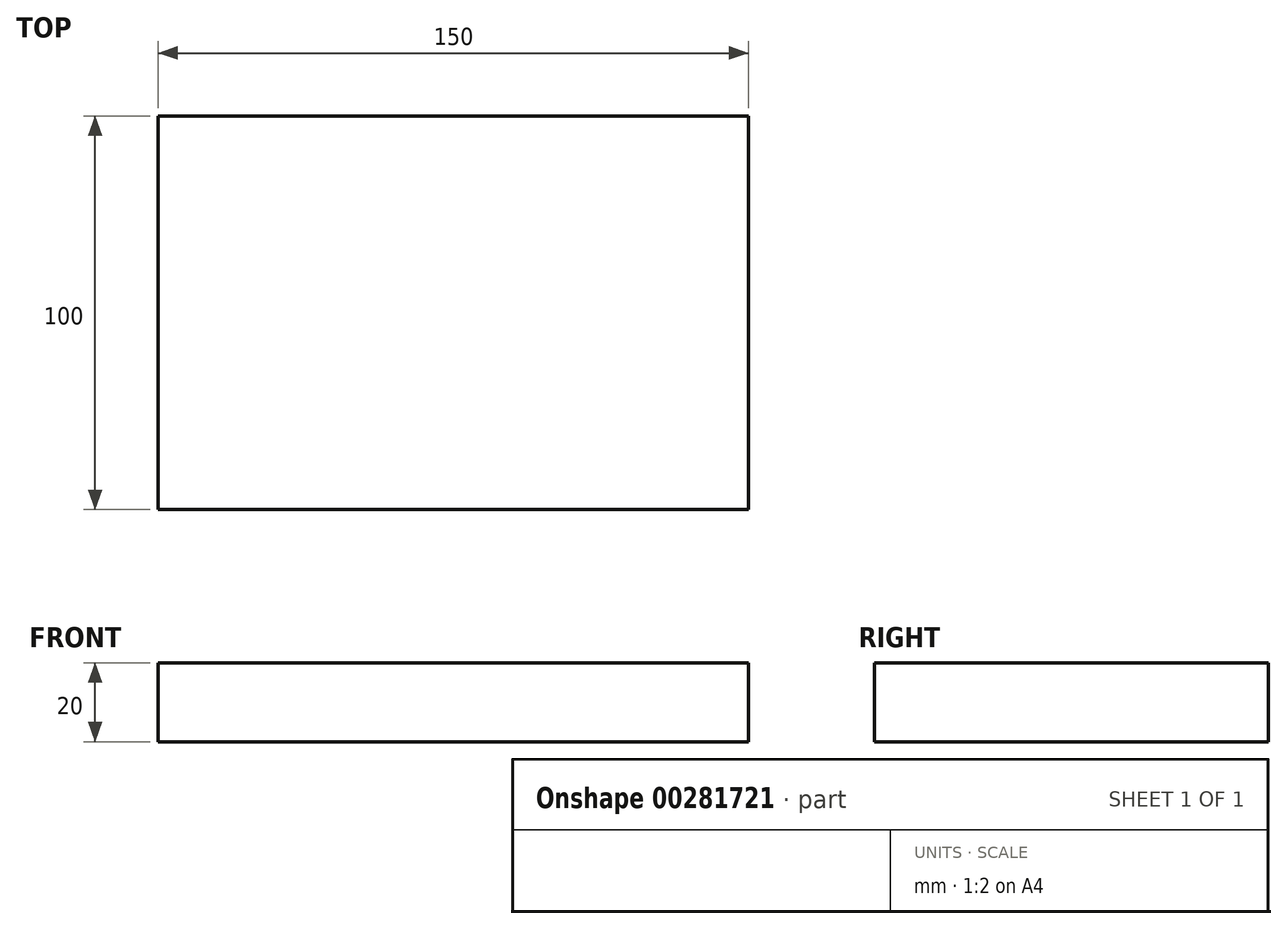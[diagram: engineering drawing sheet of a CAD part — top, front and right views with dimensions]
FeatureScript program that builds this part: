
annotation { "Feature Type Name" : "Feature", "Feature Type Description" : "" }
export const myFeature = defineFeature(function(context is Context, id is Id, definition is map)
    precondition{}
    {
        {
            var Q0;
            Q0=qCreatedBy(makeId("Top.planeOp"),FACE);
            var sketch = newSketch(context, id + "F0", { "sketchPlane" : qUnion([Q0])});
            skLineSegment(sketch, "E0.bottom", {"start": v(0, 0) * mm, "end": v(150, 0) * mm});
            skLineSegment(sketch, "E0.top", {"start": v(0, 100) * mm, "end": v(150, 100) * mm});
            skLineSegment(sketch, "E0.left", {"start": v(0, 0) * mm, "end": v(0, 100) * mm});
            skLineSegment(sketch, "E0.right", {"start": v(150, 0) * mm, "end": v(150, 100) * mm});
            skSolve(sketch);
        }
        {
            var Q0;
            Q0=makeQuery(id+"F0.imprint","IMPRINT",FACE,{"disambiguationData":[TD([[makeQuery(id+"F0.imprint","IMPRINT",EDGE,{"derivedFrom":sQuery(id+"F0.wireOp",EDGE,"E0.bottom")}),1.0]])]});
            extrude(context, id + "F1", {"entities" : qUnion([Q0]), "depth" : 20 * mm, "offsetDistance" : 25 * mm});
        }
    });
